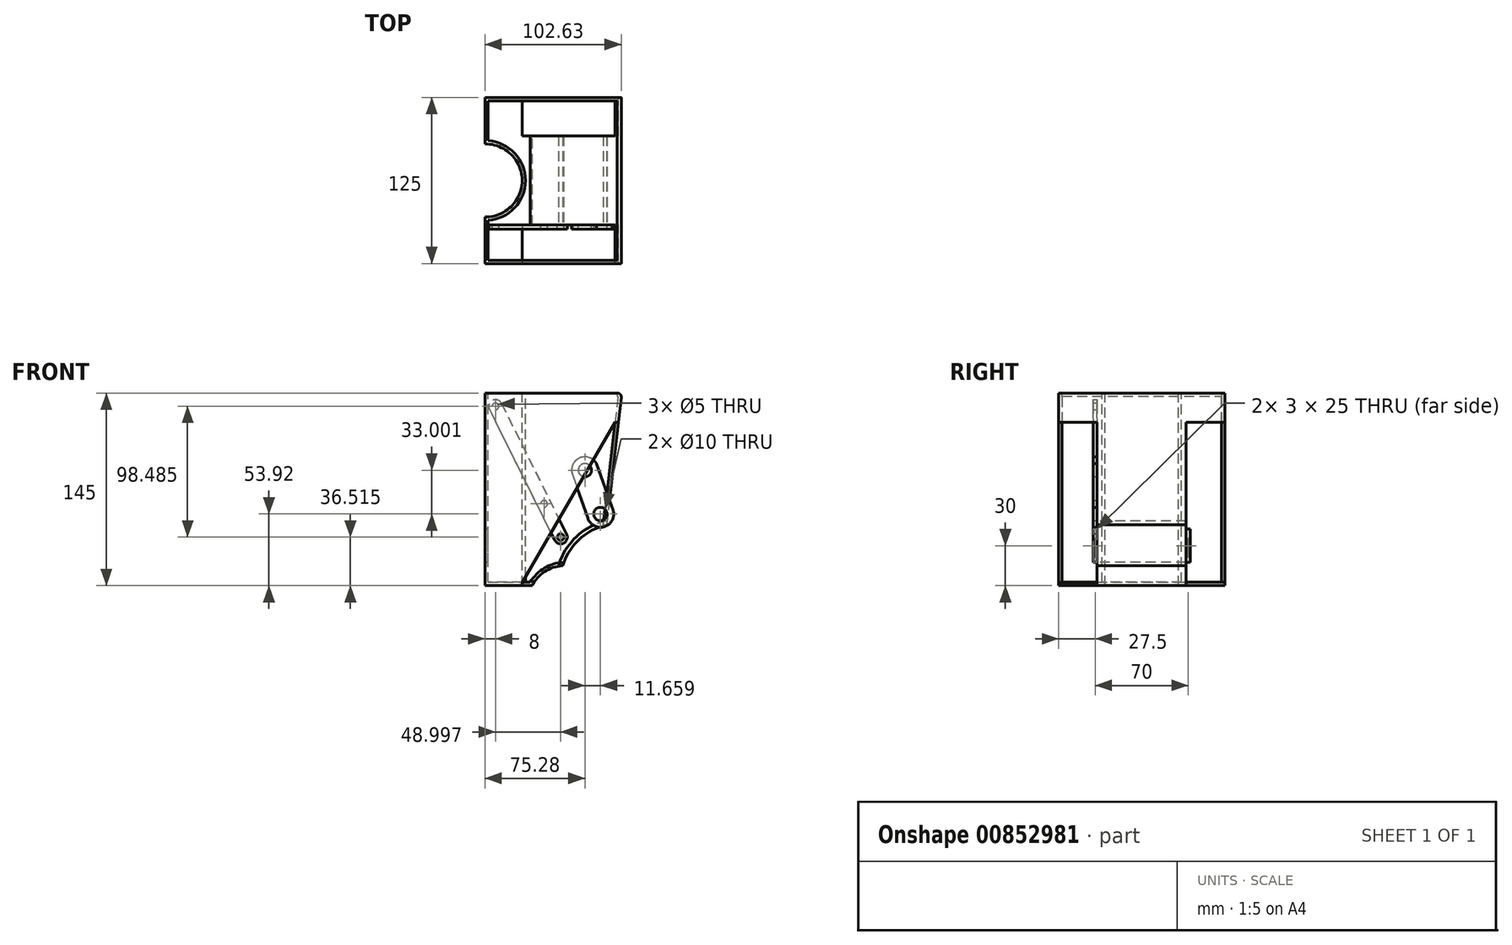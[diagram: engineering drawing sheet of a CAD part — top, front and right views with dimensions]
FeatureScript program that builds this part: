
annotation { "Feature Type Name" : "Feature", "Feature Type Description" : "" }
export const myFeature = defineFeature(function(context is Context, id is Id, definition is map)
    precondition{}
    {
        {
            var Q0;
            Q0=qCreatedBy(makeId("Front.planeOp"),FACE);
            var sketch = newSketch(context, id + "F0", { "sketchPlane" : qUnion([Q0])});
            skLineSegment(sketch, "E0", {"start": v(0, 130) * mm, "end": v(75, 130) * mm});
            skArc(sketch, "E1", {"start": v(56.58, -15) * mm, "mid": v(32.08, 0) * mm, "end": v(7.59, -15) * mm});
            skLineSegment(sketch, "E2", {"start": v(0, -15) * mm, "end": v(7.59, -15) * mm});
            skLineSegment(sketch, "E3.trimOffspring", {"start": v(56.58, -15) * mm, "end": v(58.27, -15) * mm});
            skLineSegment(sketch, "E4", {"start": v(75, 130) * mm, "end": v(58.27, -15) * mm});
            skLineSegment(sketch, "E5", {"start": v(0, 130) * mm, "end": v(-28, 130) * mm});
            skLineSegment(sketch, "E6", {"start": v(0, -15) * mm, "end": v(-28, -15) * mm});
            skLineSegment(sketch, "E7", {"start": v(-28, -15) * mm, "end": v(-28, 130) * mm});
            skLineSegment(sketch, "E8", {"start": v(75.45, 0) * mm, "end": v(-49.86, 0) * mm, "construction": true});
            skLineSegment(sketch, "E9", {"start": v(0, -37.66) * mm, "end": v(0, 158.2) * mm, "construction": true});
            skSolve(sketch);
        }
        {
            var Q0;
            Q0=makeQuery(id+"F0.imprint","IMPRINT",FACE,{"disambiguationData":[TD([[makeQuery(id+"F0.imprint","IMPRINT",EDGE,{"derivedFrom":sQuery(id+"F0.wireOp",EDGE,"AEWyvxpA-VYwD-7hNY-brtb-rKHveOHAXlaS")}),-1.0]])]});
            var Q1;
            Q1=makeQuery(id+"F0.imprint","IMPRINT",FACE,{"disambiguationData":[TD([[makeQuery(id+"F0.imprint","IMPRINT",EDGE,{"derivedFrom":sQuery(id+"F0.wireOp",EDGE,"E0")}),-1.0]])]});
            extrude(context, id + "F1", {"entities" : qUnion([Q0, Q1]), "depth" : 125 * mm, "offsetDistance" : 25 * mm});
        }
        {
            var Q0;
            Q0=makeQuery(id+"F1.opExtrude","SWEPT_FACE",FACE,{"disambiguationData":[OSD([sQuery(id+"F0.wireOp",EDGE,"E0"),sQuery(id+"F0.wireOp",EDGE,"E5")])]});
            cPlane(context, id + "F2", {"entities" : qUnion([Q0]), "cplaneType" : CPlaneType.OFFSET, "offset" : 0 * mm, "width" : 150 * mm, "height" : 150 * mm});
        }
        {
            var Q0;
            Q0=qCreatedBy(id+"F2.planeOp",FACE);
            var sketch = newSketch(context, id + "F3", { "sketchPlane" : qUnion([Q0])});
            skCircle(sketch, "E10", {"center": v(-27.5, -62.5) * mm, "radius": 27.5 * mm});
            skLineSegment(sketch, "E11", {"start": v(0, 0) * mm, "end": v(0, -125) * mm, "construction": true});
            skLineSegment(sketch, "E12", {"start": v(0, 0) * mm, "end": v(0, -62.5) * mm, "construction": true});
            skSolve(sketch);
        }
        {
            var Q0;
            Q0=makeQuery(id+"F3.imprint","IMPRINT",FACE,{"disambiguationData":[TD([[makeQuery(id+"F3.imprint","IMPRINT",EDGE,{"derivedFrom":sQuery(id+"F3.wireOp",EDGE,"E10")}),1.0]])]});
            extrude(context, id + "F4", {"entities" : qUnion([Q0]), "operationType" : NewBodyOperationType.REMOVE, "oppositeDirection" : true, "depth" : 171.8 * mm, "offsetDistance" : 25 * mm});
        }
        {
            var Q0;
            Q0=makeQuery(id+"F1.opExtrude","SWEPT_EDGE",EDGE,{"disambiguationData":[OSD([sQuery(id+"F0.wireOp",EDGE,"E0"),sQuery(id+"F0.wireOp",EDGE,"E4")])]});
            fillet(context, id + "F5", {"entities" : qUnion([Q0]), "radius" : 3 * mm, "tangentPropagation" : true, "allowEdgeOverflow" : false});
        }
        {
            var Q0;
            Q0=makeQuery(id+"F1.opExtrude","SWEPT_FACE",FACE,{"disambiguationData":[OSD([sQuery(id+"F0.wireOp",EDGE,"E0"),sQuery(id+"F0.wireOp",EDGE,"E5")])]});
            shell(context, id + "F6", {"entities" : qUnion([Q0]), "thickness" : 2.5 * mm});
        }
        {
            var Q0;
            {var subQ0=sQuery(id+"F0.wireOp",EDGE,"E7");var subQ1=sQuery(id+"F0.wireOp",EDGE,"E6");var subQ2=sQuery(id+"F0.wireOp",EDGE,"E5");var subQ3=sQuery(id+"F0.wireOp",EDGE,"E2");var subQ4=sQuery(id+"F0.wireOp",EDGE,"E0");Q0=makeQuery(id+"F4.boolean.opBoolean","SPLIT",FACE,{"disambiguationData":[TD([makeQuery(id+"F1.opExtrude","CAP_FACE",FACE,{"disambiguationData":[OSD([subQ4,sQuery(id+"F0.wireOp",EDGE,"E1"),subQ3,sQuery(id+"F0.wireOp",EDGE,"E3.trimOffspring"),sQuery(id+"F0.wireOp",EDGE,"E4"),subQ2,subQ1,subQ0])],"isStart":true})])],"derivedFrom":makeQuery(id+"F1.opExtrude","SWEPT_FACE",FACE,{"disambiguationData":[OSD([subQ0])]})});}
            cPlane(context, id + "F7", {"entities" : qUnion([Q0]), "cplaneType" : CPlaneType.OFFSET, "offset" : 0 * mm, "width" : 150 * mm, "height" : 150 * mm});
        }
        {
            var Q0;
            Q0=qCreatedBy(id+"F7.planeOp",FACE);
            var sketch = newSketch(context, id + "F8", { "sketchPlane" : qUnion([Q0])});
            skLineSegment(sketch, "E13.bottom", {"start": v(29, 2.5) * mm, "end": v(26, 2.5) * mm});
            skLineSegment(sketch, "E13.top", {"start": v(29, 27.5) * mm, "end": v(26, 27.5) * mm});
            skLineSegment(sketch, "E13.left", {"start": v(29, 2.5) * mm, "end": v(29, 27.5) * mm});
            skLineSegment(sketch, "E13.right", {"start": v(26, 2.5) * mm, "end": v(26, 27.5) * mm});
            skLineSegment(sketch, "E14.bottom", {"start": v(96, 2.5) * mm, "end": v(99, 2.5) * mm});
            skLineSegment(sketch, "E14.top", {"start": v(96, 27.5) * mm, "end": v(99, 27.5) * mm});
            skLineSegment(sketch, "E14.left", {"start": v(96, 2.5) * mm, "end": v(96, 27.5) * mm});
            skLineSegment(sketch, "E14.right", {"start": v(99, 2.5) * mm, "end": v(99, 27.5) * mm});
            skLineSegment(sketch, "E15.bottom", {"start": v(99, 2.5) * mm, "end": v(96, 2.5) * mm});
            skSolve(sketch);
        }
        {
            var Q0;
            Q0=makeQuery(id+"F8.imprint","IMPRINT",FACE,{"disambiguationData":[TD([[makeQuery(id+"F8.imprint","IMPRINT",EDGE,{"derivedFrom":sQuery(id+"F8.wireOp",EDGE,"E13.bottom")}),-1.0]])]});
            var Q1;
            Q1=makeQuery(id+"F8.imprint","IMPRINT",FACE,{"disambiguationData":[TD([[makeQuery(id+"F8.imprint","IMPRINT",EDGE,{"derivedFrom":sQuery(id+"F8.wireOp",EDGE,"E14.top")}),-1.0]])]});
            extrude(context, id + "F9", {"entities" : qUnion([Q0, Q1]), "operationType" : NewBodyOperationType.REMOVE, "oppositeDirection" : true, "depth" : 35.1 * mm, "offsetDistance" : 25 * mm});
        }
        {
            var Q0;
            Q0=qCreatedBy(id+"F7.planeOp",FACE);
            cPlane(context, id + "F10", {"entities" : qUnion([Q0]), "cplaneType" : CPlaneType.OFFSET, "offset" : 110 * mm, "oppositeDirection" : true, "width" : 150 * mm, "height" : 150 * mm});
        }
        {
            var Q0;
            Q0=qCreatedBy(id+"F10.planeOp",FACE);
            var sketch = newSketch(context, id + "F11", { "sketchPlane" : qUnion([Q0])});
            skLineSegment(sketch, "E16.bottom", {"start": v(102, -15) * mm, "end": v(99, -15) * mm});
            skLineSegment(sketch, "E16.top", {"start": v(102, 108) * mm, "end": v(99, 108) * mm});
            skLineSegment(sketch, "E16.left", {"start": v(102, -15) * mm, "end": v(102, 108) * mm});
            skLineSegment(sketch, "E16.right", {"start": v(99, -15) * mm, "end": v(99, 108) * mm});
            skLineSegment(sketch, "E17.bottom", {"start": v(26, -15) * mm, "end": v(23, -15) * mm});
            skLineSegment(sketch, "E17.top", {"start": v(26, 108) * mm, "end": v(23, 108) * mm});
            skLineSegment(sketch, "E17.left", {"start": v(26, -15) * mm, "end": v(26, 108) * mm});
            skLineSegment(sketch, "E17.right", {"start": v(23, -15) * mm, "end": v(23, 108) * mm});
            skSolve(sketch);
        }
        {
            var Q0;
            Q0=makeQuery(id+"F11.imprint","IMPRINT",FACE,{"disambiguationData":[TD([[makeQuery(id+"F11.imprint","IMPRINT",EDGE,{"derivedFrom":sQuery(id+"F11.wireOp",EDGE,"E16.bottom")}),-1.0]])]});
            var Q1;
            Q1=makeQuery(id+"F11.imprint","IMPRINT",FACE,{"disambiguationData":[TD([[makeQuery(id+"F11.imprint","IMPRINT",EDGE,{"derivedFrom":sQuery(id+"F11.wireOp",EDGE,"E17.bottom")}),-1.0]])]});
            extrude(context, id + "F12", {"entities" : qUnion([Q0, Q1]), "operationType" : NewBodyOperationType.REMOVE, "depth" : 23.73 * mm, "offsetDistance" : 25 * mm});
        }
        {
            var Q0;
            Q0=makeQuery(id+"F1.opExtrude","SWEPT_FACE",FACE,{"disambiguationData":[OSD([sQuery(id+"F0.wireOp",EDGE,"E2"),sQuery(id+"F0.wireOp",EDGE,"E6")])]});
            cPlane(context, id + "F13", {"entities" : qUnion([Q0]), "cplaneType" : CPlaneType.OFFSET, "offset" : 0 * mm, "width" : 150 * mm, "height" : 150 * mm});
        }
        {
            var Q0;
            Q0=makeQuery(id+"F1.opExtrude","CAP_FACE",FACE,{"disambiguationData":[OSD([sQuery(id+"F0.wireOp",EDGE,"E0"),sQuery(id+"F0.wireOp",EDGE,"E1"),sQuery(id+"F0.wireOp",EDGE,"E2"),sQuery(id+"F0.wireOp",EDGE,"E3.trimOffspring"),sQuery(id+"F0.wireOp",EDGE,"E4"),sQuery(id+"F0.wireOp",EDGE,"E5"),sQuery(id+"F0.wireOp",EDGE,"E6"),sQuery(id+"F0.wireOp",EDGE,"E7")])],"isStart":false});
            cPlane(context, id + "F14", {"entities" : qUnion([Q0]), "cplaneType" : CPlaneType.OFFSET, "offset" : 29 * mm, "oppositeDirection" : true, "width" : 150 * mm, "height" : 150 * mm});
        }
        {
            var Q0;
            Q0=qCreatedBy(id+"F14.planeOp",FACE);
            var sketch = newSketch(context, id + "F15", { "sketchPlane" : qUnion([Q0])});
            skCircle(sketch, "E18", {"center": v(73.93, -13.54) * mm, "radius": 45.5 * mm});
            skSolve(sketch);
        }
        {
            var Q0;
            Q0=makeQuery(id+"F15.imprint","IMPRINT",FACE,{"disambiguationData":[TD([[makeQuery(id+"F15.imprint","IMPRINT",EDGE,{"derivedFrom":sQuery(id+"F15.wireOp",EDGE,"E18")}),1.0]])]});
            var Q1;
            Q1=sQuery(id+"F15.wireOp",EDGE,"E18");
            extrude(context, id + "F16", {"entities" : qUnion([Q0]), "operationType" : NewBodyOperationType.REMOVE, "surfaceEntities" : qUnion([Q1]), "oppositeDirection" : true, "depth" : 70 * mm, "offsetDistance" : 25 * mm});
        }
        {
            var Q0;
            Q0=qCreatedBy(id+"F14.planeOp",FACE);
            var sketch = newSketch(context, id + "F17", { "sketchPlane" : qUnion([Q0])});
            skArc(sketch, "E19", {"start": v(63.52, 30.66) * mm, "mid": v(43, 19.72) * mm, "end": v(30.56, 0.06) * mm});
            skArc(sketch, "E20", {"start": v(63.89, 33.82) * mm, "mid": v(40.86, 21.83) * mm, "end": v(27.32, -0.31) * mm});
            skArc(sketch, "E21", {"start": v(30.56, 0.06) * mm, "mid": v(28.93, -0.08) * mm, "end": v(27.32, -0.31) * mm});
            skLineSegment(sketch, "E22", {"start": v(63.52, 30.66) * mm, "end": v(63.89, 33.82) * mm});
            skLineSegment(sketch, "E23", {"start": v(63.89, 33.82) * mm, "end": v(63.52, 30.66) * mm});
            skSolve(sketch);
        }
        {
            var Q0;
            Q0=qSketchRegion(id+"F17",true);
            extrude(context, id + "F18", {"entities" : qUnion([Q0]), "oppositeDirection" : true, "depth" : 70 * mm, "offsetDistance" : 25 * mm});
        }
        {
            var Q0;
            Q0=qCreatedBy(id+"F14.planeOp",FACE);
            var sketch = newSketch(context, id + "F19", { "sketchPlane" : qUnion([Q0])});
            skLineSegment(sketch, "E24", {"start": v(0, -12.59) * mm, "end": v(0, -15.04) * mm});
            skLineSegment(sketch, "E25", {"start": v(0, -15.04) * mm, "end": v(58.34, -15.04) * mm});
            skLineSegment(sketch, "E26", {"start": v(58.34, -15.04) * mm, "end": v(72.46, 108) * mm});
            skLineSegment(sketch, "E27", {"start": v(69.95, 108) * mm, "end": v(0, -12.59) * mm});
            skLineSegment(sketch, "E28", {"start": v(69.95, 108) * mm, "end": v(72.46, 108) * mm});
            skSolve(sketch);
        }
        {
            var Q0;
            Q0=makeQuery(id+"F19.imprint","IMPRINT",FACE,{"disambiguationData":[TD([[makeQuery(id+"F19.imprint","IMPRINT",EDGE,{"derivedFrom":sQuery(id+"F19.wireOp",EDGE,"E24")}),1.0]])]});
            extrude(context, id + "F20", {"entities" : qUnion([Q0]), "operationType" : NewBodyOperationType.REMOVE, "depth" : 47.2 * mm, "offsetDistance" : 25 * mm});
        }
        {
            var Q0;
            Q0=makeQuery(id+"F1.opExtrude","CAP_FACE",FACE,{"disambiguationData":[OSD([sQuery(id+"F0.wireOp",EDGE,"E0"),sQuery(id+"F0.wireOp",EDGE,"E1"),sQuery(id+"F0.wireOp",EDGE,"E2"),sQuery(id+"F0.wireOp",EDGE,"E3.trimOffspring"),sQuery(id+"F0.wireOp",EDGE,"E4"),sQuery(id+"F0.wireOp",EDGE,"E5"),sQuery(id+"F0.wireOp",EDGE,"E6"),sQuery(id+"F0.wireOp",EDGE,"E7")])],"isStart":true});
            var sketch = newSketch(context, id + "F21", { "sketchPlane" : qUnion([Q0])});
            skLineSegment(sketch, "E29", {"start": v(-72.46, 108.01) * mm, "end": v(-69.95, 108.01) * mm});
            skLineSegment(sketch, "E30", {"start": v(-69.95, 108.01) * mm, "end": v(0, -12.5) * mm});
            skLineSegment(sketch, "E31", {"start": v(0, -12.5) * mm, "end": v(0, -15) * mm});
            skLineSegment(sketch, "E32", {"start": v(0, -15) * mm, "end": v(-58.27, -15) * mm});
            skLineSegment(sketch, "E33", {"start": v(-58.27, -15) * mm, "end": v(-72.46, 108.01) * mm});
            skSolve(sketch);
        }
        {
            var Q0;
            Q0=makeQuery(id+"F21.imprint","IMPRINT",FACE,{"disambiguationData":[TD([[makeQuery(id+"F21.imprint","IMPRINT",EDGE,{"derivedFrom":sQuery(id+"F21.wireOp",EDGE,"E29")}),-1.0]])]});
            extrude(context, id + "F22", {"entities" : qUnion([Q0]), "operationType" : NewBodyOperationType.REMOVE, "oppositeDirection" : true, "depth" : 29 * mm, "offsetDistance" : 25 * mm});
        }
        {
            var Q0;
            Q0=qCreatedBy(id+"F14.planeOp",FACE);
            var sketch = newSketch(context, id + "F23", { "sketchPlane" : qUnion([Q0])});
            skArc(sketch, "E34", {"start": v(-15.52, 122.23) * mm, "mid": v(-22.23, 124.48) * mm, "end": v(-24.48, 117.77) * mm});
            skArc(sketch, "E35", {"start": v(24.52, 19.29) * mm, "mid": v(31.22, 17.04) * mm, "end": v(33.47, 23.74) * mm});
            skLineSegment(sketch, "E36", {"start": v(24.52, 19.29) * mm, "end": v(-24.48, 117.77) * mm});
            skCircle(sketch, "E37", {"center": v(-20, 120) * mm, "radius": 2.5 * mm});
            skCircle(sketch, "E38", {"center": v(29, 21.51) * mm, "radius": 2.5 * mm});
            skCircle(sketch, "E39", {"center": v(16.52, 46.58) * mm, "radius": 2.5 * mm});
            skLineSegment(sketch, "E40", {"start": v(-15.52, 122.23) * mm, "end": v(33.47, 23.74) * mm});
            skArc(sketch, "E41", {"start": v(77.88, 91.62) * mm, "mid": v(70.84, 92.51) * mm, "end": v(70, 85.47) * mm});
            skCircle(sketch, "E42", {"center": v(73.92, 88.57) * mm, "radius": 2.5 * mm});
            skArc(sketch, "E43", {"start": v(82.16, 69.68) * mm, "mid": v(89.17, 68.77) * mm, "end": v(90.08, 75.78) * mm});
            skCircle(sketch, "E44", {"center": v(86.12, 72.73) * mm, "radius": 2.5 * mm});
            skLineSegment(sketch, "E45", {"start": v(77.88, 91.62) * mm, "end": v(90.08, 75.78) * mm});
            skLineSegment(sketch, "E46", {"start": v(70, 85.47) * mm, "end": v(82.16, 69.68) * mm});
            skSolve(sketch);
        }
        {
            var Q0;
            {var subQ0=sQuery(id+"F23.wireOp",EDGE,"CEpgBrpP-yiiY-twuG-gih4-8btHfCE1UIKM");Q0=makeQuery(id+"F23.imprint","IMPRINT",FACE,{"disambiguationData":[TD([[makeQuery(id+"F23.imprint","IMPRINT",EDGE,{"derivedFrom":subQ0}),-1.0]])]});}
            var Q1;
            Q1=makeQuery(id+"F23.imprint","IMPRINT",FACE,{"disambiguationData":[TD([[makeQuery(id+"F23.imprint","IMPRINT",EDGE,{"derivedFrom":sQuery(id+"F23.wireOp",EDGE,"E38")}),-1.0]])]});
            var Q2;
            Q2=makeQuery(id+"F23.imprint","IMPRINT",FACE,{"disambiguationData":[TD([[makeQuery(id+"F23.imprint","IMPRINT",EDGE,{"derivedFrom":sQuery(id+"F23.wireOp",EDGE,"E37")}),-1.0]])]});
            extrude(context, id + "F24", {"entities" : qUnion([Q0, Q1, Q2]), "depth" : 3 * mm, "offsetDistance" : 25 * mm});
        }
        {
            var Q0;
            Q0=qCreatedBy(id+"F14.planeOp",FACE);
            var sketch = newSketch(context, id + "F25", { "sketchPlane" : qUnion([Q0])});
            skCircle(sketch, "E47", {"center": v(47.28, 71.92) * mm, "radius": 5 * mm});
            skCircle(sketch, "E48", {"center": v(58.94, 38.92) * mm, "radius": 5 * mm});
            skLineSegment(sketch, "E49.0", {"start": v(56.02, 76.78) * mm, "end": v(67.68, 43.78) * mm});
            skArc(sketch, "E50", {"start": v(56.02, 76.78) * mm, "mid": v(42.42, 80.66) * mm, "end": v(38.54, 67.06) * mm});
            skArc(sketch, "E51", {"start": v(49.5, 35.63) * mm, "mid": v(63.03, 29.8) * mm, "end": v(67.68, 43.78) * mm});
            skLineSegment(sketch, "E52", {"start": v(38.54, 67.06) * mm, "end": v(49.5, 35.63) * mm});
            skSolve(sketch);
        }
        {
            var Q0;
            Q0=makeQuery(id+"F25.imprint","IMPRINT",FACE,{"disambiguationData":[TD([[makeQuery(id+"F25.imprint","IMPRINT",EDGE,{"derivedFrom":sQuery(id+"F25.wireOp",EDGE,"11HY7FTl-I5bV-LVFI-AWjC-FNhEUOHaCupe")}),1.0]])]});
            var Q1;
            Q1=makeQuery(id+"F25.imprint","IMPRINT",FACE,{"disambiguationData":[TD([[makeQuery(id+"F25.imprint","IMPRINT",EDGE,{"derivedFrom":sQuery(id+"F25.wireOp",EDGE,"E47")}),-1.0]])]});
            extrude(context, id + "F26", {"entities" : qUnion([Q0, Q1]), "depth" : 3 * mm, "offsetDistance" : 25 * mm});
        }
    });
